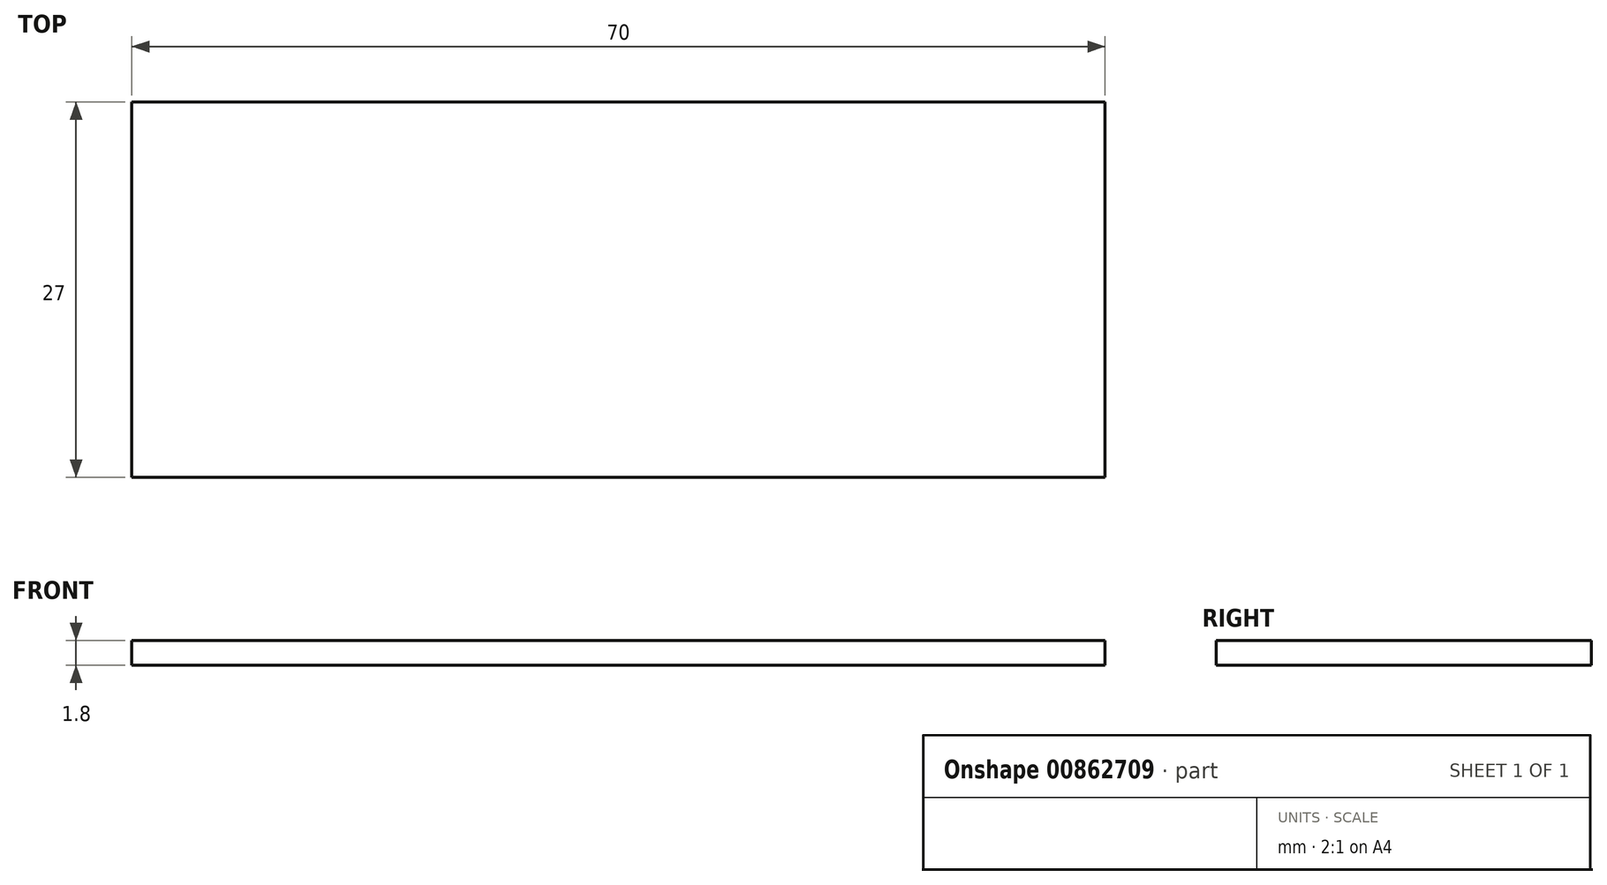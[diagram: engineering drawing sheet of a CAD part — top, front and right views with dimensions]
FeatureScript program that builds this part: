
annotation { "Feature Type Name" : "Feature", "Feature Type Description" : "" }
export const myFeature = defineFeature(function(context is Context, id is Id, definition is map)
    precondition{}
    {
        {
            var Q0;
            Q0=qCreatedBy(makeId("Top.planeOp"),FACE);
            var sketch = newSketch(context, id + "F0", { "sketchPlane" : qUnion([Q0])});
            skLineSegment(sketch, "E0.bottom", {"start": v(0, 0) * mm, "end": v(70, 0) * mm});
            skLineSegment(sketch, "E0.top", {"start": v(0, -27) * mm, "end": v(70, -27) * mm});
            skLineSegment(sketch, "E0.left", {"start": v(0, 0) * mm, "end": v(0, -27) * mm});
            skLineSegment(sketch, "E0.right", {"start": v(70, 0) * mm, "end": v(70, -27) * mm});
            skSolve(sketch);
        }
        {
            var Q0;
            Q0=makeQuery(id+"F0.imprint","IMPRINT",FACE,{"disambiguationData":[TD([[makeQuery(id+"F0.imprint","IMPRINT",EDGE,{"derivedFrom":sQuery(id+"F0.wireOp",EDGE,"E0.bottom")}),-1.0]])]});
            extrude(context, id + "F1", {"entities" : qUnion([Q0]), "depth" : 1.8 * mm, "offsetDistance" : 25 * mm});
        }
    });
